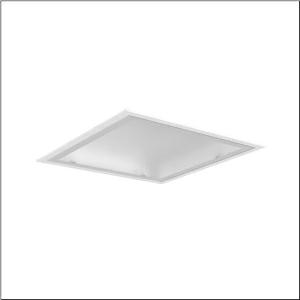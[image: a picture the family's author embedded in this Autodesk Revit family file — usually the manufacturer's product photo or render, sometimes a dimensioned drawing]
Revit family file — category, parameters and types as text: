
# Revit family: mira_11_51fr127a461a
name_source: partatom
category: Lighting Fixtures
units: mm (PartAtom-declared; Revit-internal decimal feet)

## family parameters
Cut with Voids When Loaded = No
Host = Face
Light Source = No
Part Type = Normal
Room Calculation Point = No
Round Connector Dimension = Use Diameter
Shared = No

## types (1)
- Mira 11 (1 x LED, 6100 lm, 53 W, 4000K)
    Apparent Load = 53 VA
    CIE Flux Codes = 51 82 97 100 100
    Color Rendering = 80
    Color Temperature = 4000K
    Default Elevation = 1800 mm
    Description = Mira 11, clean room luminaire, primary light control with reflector, primary optical cover: cover, of toughened safety glass, light emission: direct distribution, primary light characteristic: symmetric, installation type: recessed, LED, rated luminous flux: 6.100lm, luminous efficacy: 115lm/W, light colour: 840, colour temperature: 4000K, control gear: ON/OFF, with terminal, 3-pole, max. 2.5mm², mains connection: 230V, AC, 50/60Hz, rated input power: 53W, luminaire housing, of sheet steel, coated, pure white (RAL 9010), with concealed magnets, module: M625, length: 623mm, width: 623mm, height: 90mm, protection rating (complete): IP65, insulation class (complete): insulation class I (protective earthing), certification: CE, UKCA, permissible operating ambient temperature: -5..+40°C, standard: EN 50419, packaging unit: 1 piece
    Height = 0 mm  [stored 0 ft]
    Lamp = 1 x LED
    Lamp Light Flux = 6100 lm
    Lamp Power = 53 W
    Lamp count = 1
    Length = 625 mm
    Luminous efficacy = 115 lm/W
    Manufacturer = Siteco
    ModVariant = No
    Model = 51FR127A461A
    Mounting Place = Ceiling
    Mounting Type = Recessed
    Number of Poles = 1
    OnlyDefault = Yes
    Power Factor = 1
    Product Name = Mira 11
    Product group = clean room luminaire | ceiling recessed
    ProductGroupID = 402
    Protection Class = Protection class I
    Protection Degree = IP 65
    RLX_Detail_Level = 1
    RLX_Emergency_Light_Flux = 0 lm
    RLX_Emergency_Type = 0
    RLX_Emergency_Type_DB = No
    RlxData = <blob elided: 19257 chars, md5=c1c34a70>
    Socket = socket
    Standby Power = 0 W
    System Light Flux = 6100 lm
    System Power = 53 W
    Type Comments = Product without accessories
    Type Image = l_1006636.jpg
    URL = http://relux.com
    VarID = ---
    Voltage = 0 V
    Weight = 0.00 kg
    Width = 625 mm

note: [stored X ft] marks values corroborated as IEEE doubles in the binary element streams (Revit-internal decimal feet)

## geometry (parser evidence)
native form markers: Blend x4, Sweep x11
no freeform markers — native parametric forms only
